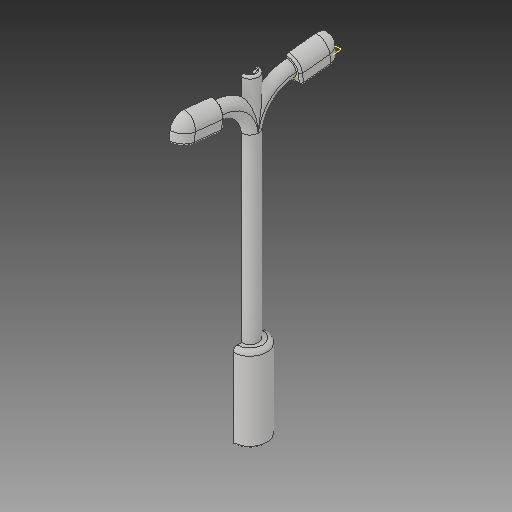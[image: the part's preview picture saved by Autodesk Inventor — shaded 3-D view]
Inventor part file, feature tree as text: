
AUTODESK INVENTOR PART (.ipt)
format: ipt  version: 2018 (Build 220112000, 112)  size: 350,720 bytes
history: native  units: in
note: dims shown in document units (in); Inventor stores cm internally (conversion verified against a paired STEP export)
features: sketch x11, other x3, plane x1
ambient origin geometry x8: Origin, YZ Plane, XZ Plane, XY Plane, X Axis, Y Axis, Z Axis, Center Point
bodies: Solid1 (feature_tree)
feature tree (15):
  other  "lampa_dual.ipt"
  other  "Solid1::lampa_dual.ipt"
  other  "TaggingFeature1"
  sketch  "Sketch1"  dims[d0=0.3937in]
  sketch  "Sketch6"
  sketch  "Sketch8"
  sketch  "Sketch9"
  sketch  "Sketch10"
  sketch  "Sketch11"
  sketch  "Sketch12"
  sketch  "Sketch13"
  sketch  "Sketch14"
  sketch  "Sketch15"
  sketch  "Sketch16"
  plane  "Work Plane1"
